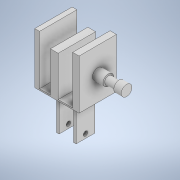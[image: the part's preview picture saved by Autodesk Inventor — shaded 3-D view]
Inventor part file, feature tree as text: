
AUTODESK INVENTOR PART (.ipt)
format: ipt  version: 2020 (Build 240168000, 168)  size: 173,568 bytes
history: native  units: mm
features: extrude x6, sketch x6
ambient origin geometry x8: Origin, YZ Plane, XZ Plane, XY Plane, X Axis, Y Axis, Z Axis, Center Point
bodies: Solid1 (feature_tree)
feature tree (12):
  extrude  "Extrusion1"  TaperAngle=0.0deg  [1 undecoded]
  extrude  "Extrusion2"  Depth=35.0mm TaperAngle=0.0deg
  extrude  "Extrusion3"  Depth=35.0mm
  extrude  "Extrusion4"  TaperAngle=0.0deg  [1 undecoded]
  extrude  "Extrusion5"  [1 undecoded]
  extrude  "Extrusion6"  [1 undecoded]
  sketch  "Sketch1"  dims[d10=0.0mm d14=0.0mm]
  sketch  "Sketch2"  dims[d16=23.0mm d20=35.0mm d21=0.0mm]
  sketch  "Sketch3"  dims[d22=35.0mm d23=0.0mm d26=46.312mm]
  sketch  "Sketch4"  dims[d27=19.946mm d28=0.0mm d31=0.0mm]
  sketch  "Sketch5"  dims[d34=0.0mm]
  sketch  "Sketch6"
note: 4 required parameter values undecoded (feature->parameter linkage not recoverable at this tier; creation-order binding heuristic only, values carry confidence <= 0.55)
